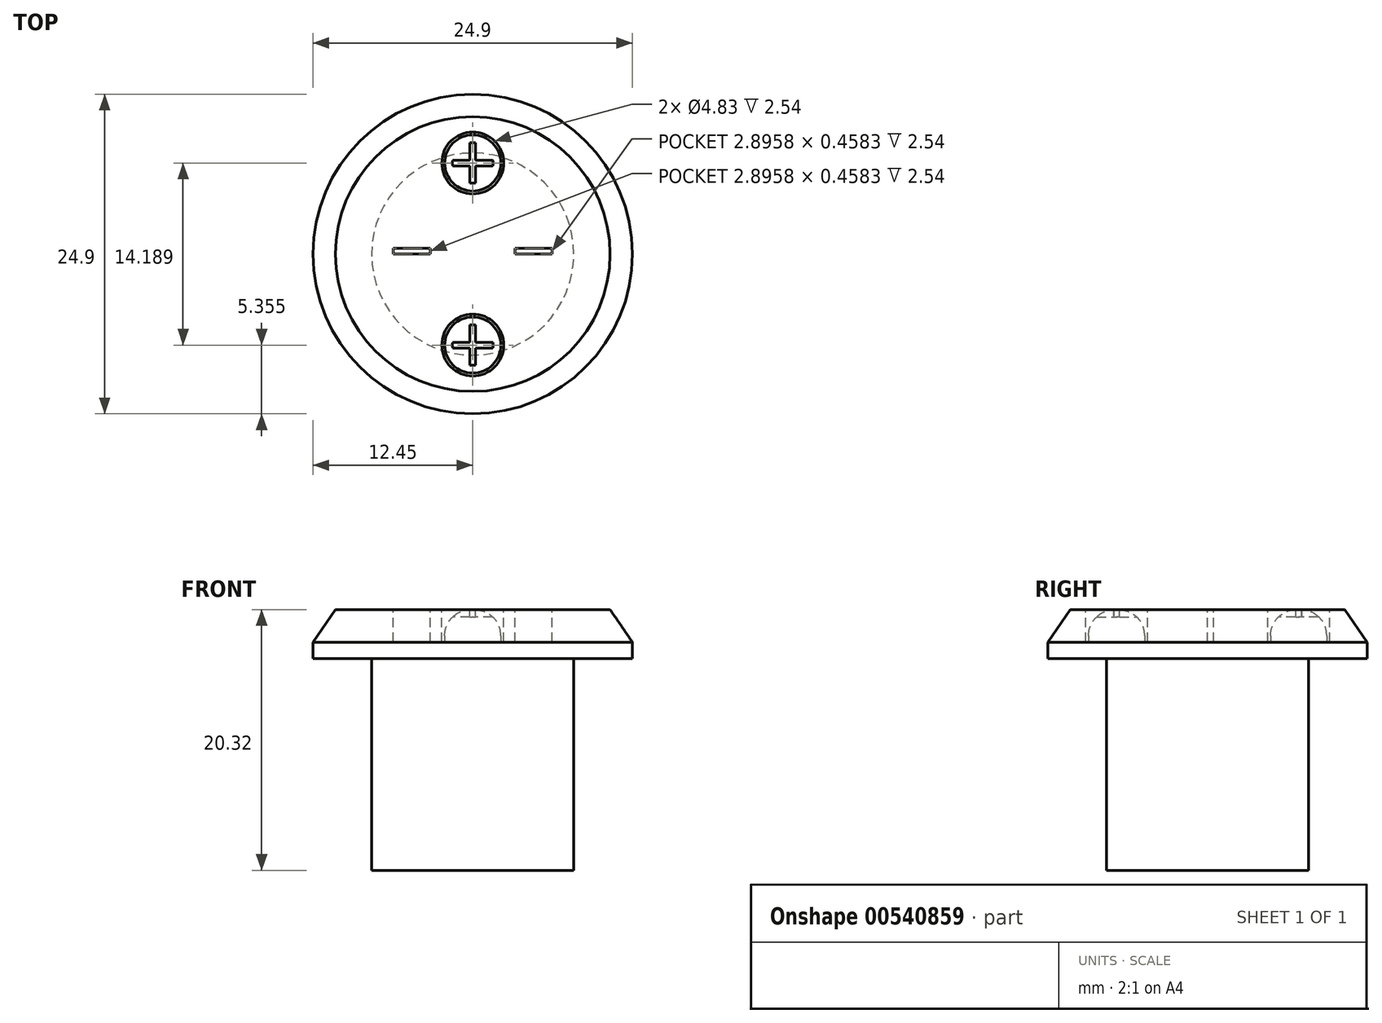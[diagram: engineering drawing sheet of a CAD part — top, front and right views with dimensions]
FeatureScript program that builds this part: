
annotation { "Feature Type Name" : "Feature", "Feature Type Description" : "" }
export const myFeature = defineFeature(function(context is Context, id is Id, definition is map)
    precondition{}
    {
        {
            var Q0;
            Q0=qCreatedBy(makeId("Top.planeOp"),FACE);
            var sketch = newSketch(context, id + "F0", { "sketchPlane" : qUnion([Q0])});
            skCircle(sketch, "E0", {"center": v(0, 0) * mm, "radius": 12.45 * mm});
            skSolve(sketch);
        }
        {
            var Q0;
            Q0 = qSketchRegion(id + "F0", true);
            extrude(context, id + "F1", {"entities" : qUnion([Q0]), "oppositeDirection" : true, "depth" : 1.27 * mm, "offsetDistance" : 25.4 * mm});
        }
        {
            var Q0;
            Q0=makeQuery(id+"F1.opExtrude","CAP_FACE",FACE,{"disambiguationData":[OSD([sQuery(id+"F0.wireOp",EDGE,"E0")])],"isStart":true});
            cPlane(context, id + "F2", {"entities" : qUnion([Q0]), "cplaneType" : CPlaneType.OFFSET, "offset" : 2.54 * mm, "width" : 152.4 * mm, "height" : 152.4 * mm});
        }
        {
            var Q0;
            Q0=qCreatedBy(id+"F2.planeOp",FACE);
            var sketch = newSketch(context, id + "F3", { "sketchPlane" : qUnion([Q0])});
            skCircle(sketch, "E1", {"center": v(0, 0) * mm, "radius": 10.7 * mm});
            skSolve(sketch);
        }
        {
            var Q1;
            Q1=makeQuery(id+"F1.opExtrude","CAP_FACE",FACE,{"disambiguationData":[OSD([sQuery(id+"F0.wireOp",EDGE,"E0")])],"isStart":true});
            var Q2;
            Q2=makeQuery(id+"F3.imprint","IMPRINT",FACE,{"disambiguationData":[TD([[makeQuery(id+"F3.imprint","IMPRINT",EDGE,{"derivedFrom":sQuery(id+"F3.wireOp",EDGE,"E1")}),1.0]])]});
            loft(context, id + "F4", {"operationType" : NewBodyOperationType.ADD, "sheetProfilesArray" : [{ "sheetProfileEntities" : qUnion([Q1]) }, { "sheetProfileEntities" : qUnion([Q2]) }]});
        }
        {
            var Q0;
            Q0=makeQuery(id+"F4.opLoft","CAP_FACE",FACE,{"disambiguationData":[OSD([makeQuery(id+"F3.imprint","IMPRINT",FACE,{"disambiguationData":[TD([[makeQuery(id+"F3.imprint","IMPRINT",EDGE,{"derivedFrom":sQuery(id+"F3.wireOp",EDGE,"E1")}),1.0]])]})])],"isStart":true});
            var sketch = newSketch(context, id + "F5", { "sketchPlane" : qUnion([Q0])});
            skCircle(sketch, "E2", {"center": v(0, 7.1) * mm, "radius": 2.42 * mm});
            skCircle(sketch, "E3.1.0", {"center": v(0, -7.1) * mm, "radius": 2.42 * mm});
            skPoint(sketch, "E3.center", {"position": v(0, 0) * mm});
            skSolve(sketch);
        }
        {
            var Q0;
            Q0 = qSketchRegion(id + "F5", true);
            extrude(context, id + "F6", {"entities" : qUnion([Q0]), "operationType" : NewBodyOperationType.REMOVE, "oppositeDirection" : true, "depth" : 2.54 * mm, "offsetDistance" : 25.4 * mm});
        }
        {
            var Q0;
            Q0=makeQuery(id+"F6.boolean.opBoolean","COPY",FACE,{"derivedFrom":makeQuery(id+"F6.opExtrude","CAP_FACE",FACE,{"disambiguationData":[OSD([sQuery(id+"F5.wireOp",EDGE,"E2")])],"isStart":false})});
            var sketch = newSketch(context, id + "F7", { "sketchPlane" : qUnion([Q0])});
            skCircle(sketch, "E4", {"center": v(0, 7.1) * mm, "radius": 2.19 * mm});
            skCircle(sketch, "E5.1.0", {"center": v(0, -7.1) * mm, "radius": 2.19 * mm});
            skPoint(sketch, "E5.center", {"position": v(0, 0) * mm});
            skSolve(sketch);
        }
        {
            var Q0;
            Q0 = qSketchRegion(id + "F7", true);
            extrude(context, id + "F8", {"entities" : qUnion([Q0]), "operationType" : NewBodyOperationType.ADD, "depth" : 2.54 * mm, "offsetDistance" : 25.4 * mm});
        }
        {
            var Q0;
            Q0=makeQuery(id+"F8.opExtrude","CAP_EDGE",EDGE,{"disambiguationData":[OSD([sQuery(id+"F7.wireOp",EDGE,"E4")])],"isStart":false});
            var Q1;
            Q1=makeQuery(id+"F8.opExtrude","CAP_FACE",FACE,{"disambiguationData":[OSD([sQuery(id+"F7.wireOp",EDGE,"E5.1.0")])],"isStart":false});
            fillet(context, id + "F9", {"entities" : qUnion([Q0, Q1]), "radius" : 2.03 * mm, "tangentPropagation" : true, "allowEdgeOverflow" : false});
        }
        {
            var Q0;
            Q0=makeQuery(id+"F8.opExtrude","CAP_FACE",FACE,{"disambiguationData":[OSD([sQuery(id+"F7.wireOp",EDGE,"E4")])],"isStart":false});
            var sketch = newSketch(context, id + "F10", { "sketchPlane" : qUnion([Q0])});
            skLineSegment(sketch, "E6.bottom", {"start": v(-0.22, 8.67) * mm, "end": v(0.22, 8.67) * mm});
            skLineSegment(sketch, "E6.top", {"start": v(-0.22, 5.51) * mm, "end": v(0.22, 5.51) * mm});
            skLineSegment(sketch, "E6.left", {"start": v(-0.22, 8.67) * mm, "end": v(-0.22, 7.31) * mm});
            skLineSegment(sketch, "E6.right", {"start": v(0.22, 8.67) * mm, "end": v(0.22, 7.31) * mm});
            skPoint(sketch, "E6.middle", {"position": v(0, 7.1) * mm});
            skLineSegment(sketch, "E7.1.0", {"start": v(1.58, 6.87) * mm, "end": v(0.22, 6.87) * mm});
            skLineSegment(sketch, "E7.1.1", {"start": v(1.58, 7.31) * mm, "end": v(1.58, 6.87) * mm});
            skLineSegment(sketch, "E7.1.2", {"start": v(1.58, 7.31) * mm, "end": v(0.22, 7.31) * mm});
            skLineSegment(sketch, "E7.1.3", {"start": v(-1.58, 7.31) * mm, "end": v(-1.58, 6.87) * mm});
            skLineSegment(sketch, "E7.anchor1", {"start": v(0, 7.1) * mm, "end": v(0.22, 5.51) * mm, "construction": true});
            skLineSegment(sketch, "E7.anchor2", {"start": v(0, 7.1) * mm, "end": v(-1.58, 6.87) * mm, "construction": true});
            skLineSegment(sketch, "E8.trimOffspring", {"start": v(-0.22, 6.87) * mm, "end": v(-0.22, 5.51) * mm});
            skLineSegment(sketch, "E9.trimOffspring", {"start": v(-0.22, 7.31) * mm, "end": v(-1.58, 7.31) * mm});
            skLineSegment(sketch, "E10.trimOffspring", {"start": v(0.22, 6.87) * mm, "end": v(0.22, 5.51) * mm});
            skLineSegment(sketch, "E11.trimOffspring", {"start": v(-0.22, 6.87) * mm, "end": v(-1.58, 6.87) * mm});
            skLineSegment(sketch, "E12.1.0", {"start": v(0.22, -6.87) * mm, "end": v(1.58, -6.87) * mm});
            skLineSegment(sketch, "E12.1.1", {"start": v(1.58, -7.31) * mm, "end": v(1.58, -6.87) * mm});
            skLineSegment(sketch, "E12.1.2", {"start": v(0, -7.1) * mm, "end": v(-0.22, -5.51) * mm, "construction": true});
            skLineSegment(sketch, "E12.1.3", {"start": v(0, -7.1) * mm, "end": v(1.58, -6.87) * mm, "construction": true});
            skLineSegment(sketch, "E12.1.4", {"start": v(0.22, -6.87) * mm, "end": v(0.22, -5.51) * mm});
            skLineSegment(sketch, "E12.1.5", {"start": v(-0.22, -6.87) * mm, "end": v(-0.22, -5.51) * mm});
            skLineSegment(sketch, "E12.1.6", {"start": v(0.22, -7.31) * mm, "end": v(1.58, -7.31) * mm});
            skLineSegment(sketch, "E12.1.7", {"start": v(-1.58, -6.87) * mm, "end": v(-0.22, -6.87) * mm});
            skLineSegment(sketch, "E12.1.8", {"start": v(-0.22, -8.67) * mm, "end": v(-0.22, -7.31) * mm});
            skLineSegment(sketch, "E12.1.9", {"start": v(0.22, -8.67) * mm, "end": v(0.22, -7.31) * mm});
            skLineSegment(sketch, "E12.1.10", {"start": v(-1.58, -7.31) * mm, "end": v(-0.22, -7.31) * mm});
            skPoint(sketch, "E12.1.11", {"position": v(0, -7.1) * mm});
            skLineSegment(sketch, "E12.1.12", {"start": v(-1.58, -7.31) * mm, "end": v(-1.58, -6.87) * mm});
            skLineSegment(sketch, "E12.1.13", {"start": v(0.22, -5.51) * mm, "end": v(-0.22, -5.51) * mm});
            skLineSegment(sketch, "E12.1.14", {"start": v(0.22, -8.67) * mm, "end": v(-0.22, -8.67) * mm});
            skPoint(sketch, "E12.1.15", {"position": v(0, -7.1) * mm});
            skPoint(sketch, "E12.center", {"position": v(0, 0) * mm});
            skSolve(sketch);
        }
        {
            var Q0;
            Q0 = qSketchRegion(id + "F10", true);
            var Q1;
            Q1=makeQuery(id+"F9.opFillet","BLEND_FACE",FACE,{"disambiguationData":[OSD([sQuery(id+"F7.wireOp",EDGE,"E4")])]});
            var Q2;
            Q2=makeQuery(id+"F1.opExtrude","SWEPT_BODY",BODY,{"disambiguationData":[OSD([sQuery(id+"F0.wireOp",EDGE,"E0")])]});
            extrude(context, id + "F11", {"entities" : qUnion([Q0]), "operationType" : NewBodyOperationType.REMOVE, "oppositeDirection" : true, "depth" : 0.58 * mm, "endBoundEntityFace" : qUnion([Q1]), "endBoundEntityBody" : qUnion([Q2]), "offsetDistance" : 25.4 * mm});
        }
        {
            var Q0;
            Q0=makeQuery(id+"F4.opLoft","CAP_FACE",FACE,{"disambiguationData":[OSD([makeQuery(id+"F3.imprint","IMPRINT",FACE,{"disambiguationData":[TD([[makeQuery(id+"F3.imprint","IMPRINT",EDGE,{"derivedFrom":sQuery(id+"F3.wireOp",EDGE,"E1")}),1.0]])]})])],"isStart":true});
            var sketch = newSketch(context, id + "F12", { "sketchPlane" : qUnion([Q0])});
            skLineSegment(sketch, "E13.bottom", {"start": v(-3.3, 0) * mm, "end": v(-6.2, 0) * mm});
            skLineSegment(sketch, "E13.top", {"start": v(-3.3, 0.46) * mm, "end": v(-6.2, 0.46) * mm});
            skLineSegment(sketch, "E13.left", {"start": v(-3.3, 0) * mm, "end": v(-3.3, 0.46) * mm});
            skLineSegment(sketch, "E13.right", {"start": v(-6.2, 0) * mm, "end": v(-6.2, 0.46) * mm});
            skLineSegment(sketch, "E14.MirrorCS", {"start": v(6.2, 0) * mm, "end": v(6.2, 0.46) * mm});
            skLineSegment(sketch, "E15.MirrorCS", {"start": v(3.3, 0) * mm, "end": v(3.3, 0.46) * mm});
            skLineSegment(sketch, "E16.MirrorCS", {"start": v(3.3, 0.46) * mm, "end": v(6.2, 0.46) * mm});
            skLineSegment(sketch, "E17.MirrorCS", {"start": v(3.3, 0) * mm, "end": v(6.2, 0) * mm});
            skSolve(sketch);
        }
        {
            var Q0;
            Q0 = qSketchRegion(id + "F12", true);
            extrude(context, id + "F13", {"entities" : qUnion([Q0]), "operationType" : NewBodyOperationType.REMOVE, "oppositeDirection" : true, "depth" : 2.54 * mm, "offsetDistance" : 25.4 * mm});
        }
        {
            var Q0;
            Q0=makeQuery(id+"F1.opExtrude","CAP_FACE",FACE,{"disambiguationData":[OSD([sQuery(id+"F0.wireOp",EDGE,"E0")])],"isStart":false});
            var sketch = newSketch(context, id + "F14", { "sketchPlane" : qUnion([Q0])});
            skCircle(sketch, "E18", {"center": v(0, 0) * mm, "radius": 7.87 * mm});
            skSolve(sketch);
        }
        {
            var Q0;
            Q0 = qSketchRegion(id + "F14", true);
            extrude(context, id + "F15", {"entities" : qUnion([Q0]), "operationType" : NewBodyOperationType.ADD, "depth" : 16.5 * mm, "offsetDistance" : 25.4 * mm});
        }
    });
